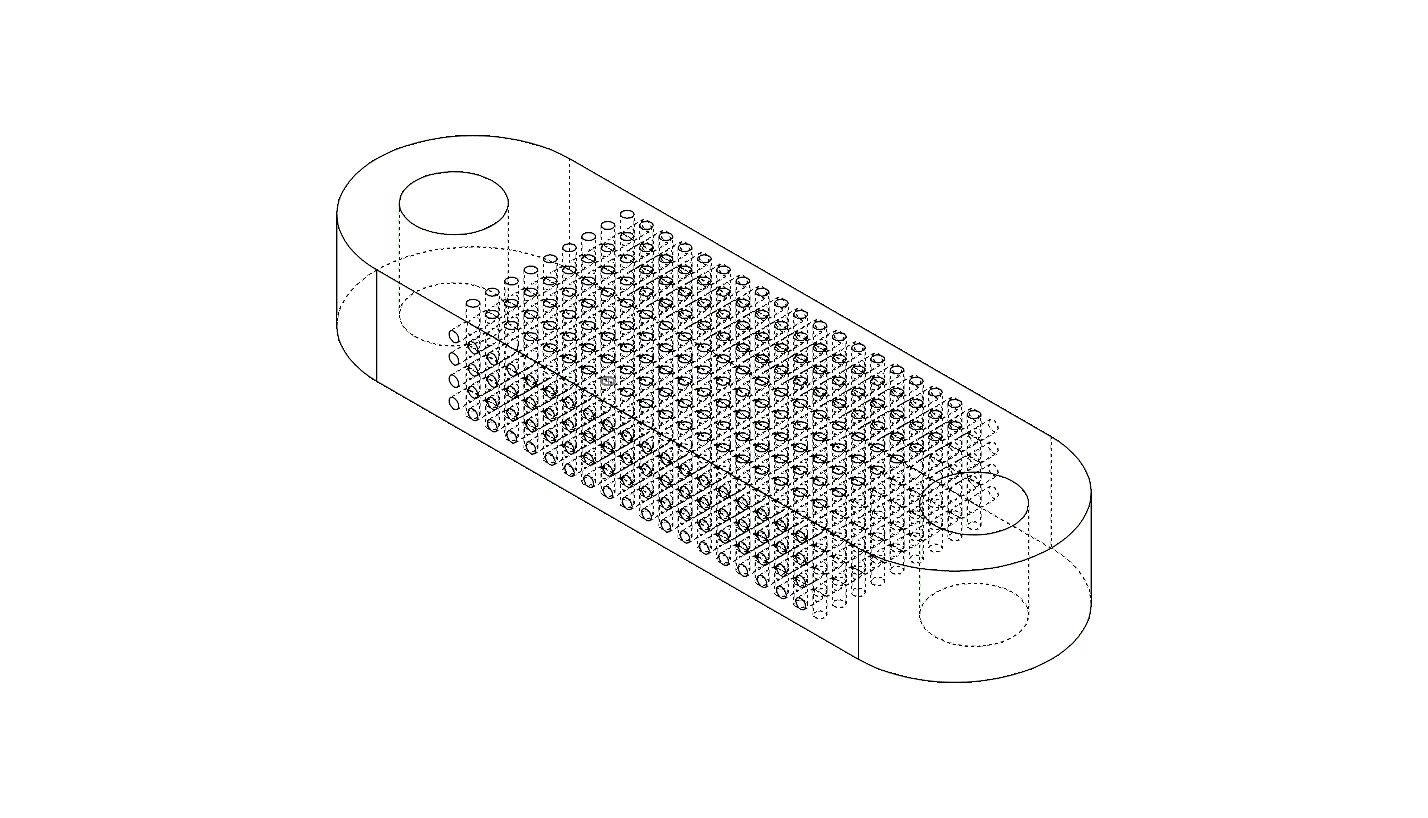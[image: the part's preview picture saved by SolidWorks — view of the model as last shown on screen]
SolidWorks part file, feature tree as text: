
SOLIDWORKS PART (.sldprt)
format: sldprt  version: not decoded by parser v0  size: 1,117,184 bytes
history: native  units: mm
features: sketch x24, cut_extrude x20, pattern_linear x10, extrude x3, material x1 (+13 scaffold rows collapsed)
feature tree (71):
  scaffold x13  (default folders/planes/origin — collapsed)
  material  "Material <not specified>"
  sketch  "Sketch1"
  extrude  "Boss-Extrude1"  Depth=10mm
  sketch  "Sketch2"  dims[D1=~7.810507mm]
  extrude  "Boss-Extrude2"  Depth=10mm
  sketch  "Sketch3"  dims[D1=~9.359973mm]
  extrude  "Boss-Extrude3"  Depth=10mm
  sketch  "Sketch4"  dims[D1=8.0mm]
  cut_extrude  "Cut-Extrude1"  [1 undecoded]
  sketch  "Sketch5"  dims[D1=~3.853714mm]
  cut_extrude  "Cut-Extrude2"  [1 undecoded]
  sketch  "Sketch6"  dims[D1=~0.81725mm]
  cut_extrude  "Cut-Extrude3"  [1 undecoded]
  sketch  "Sketch7"  dims[D1=~1.056004mm]
  cut_extrude  "Cut-Extrude4"  [1 undecoded]
  sketch  "Sketch8"  dims[D1=~0.821133mm]
  cut_extrude  "Cut-Extrude5"  [1 undecoded]
  sketch  "Sketch9"  dims[D1=~1.176837mm]
  cut_extrude  "Cut-Extrude6"  [1 undecoded]
  sketch  "Sketch10"  dims[D1=~0.670574mm]
  cut_extrude  "Cut-Extrude7"  [1 undecoded]
  sketch  "Sketch11"  dims[D1=~0.862768mm]
  cut_extrude  "Cut-Extrude8"  Depth=10mm
  sketch  "Sketch12"  dims[D1=~0.725265mm]
  cut_extrude  "Cut-Extrude9"  [1 undecoded]
  sketch  "Sketch13"  dims[D1=~0.63802mm]
  cut_extrude  "Cut-Extrude10"  [1 undecoded]
  sketch  "Sketch14"  dims[D1=~1.61086mm]
  sketch  "Sketch15"  dims[D1=~0.437297mm]
  cut_extrude  "Cut-Extrude14"  [1 undecoded]
  pattern_linear  "LPattern2"  Count1=1 Count2=11 Spacing1=2mm Spacing2=2mm
  sketch  "Sketch16"  dims[D1=~0.443199mm]
  cut_extrude  "Cut-Extrude15"  [1 undecoded]
  pattern_linear  "LPattern3"  Count1=19 Count2=1 Spacing1=2mm Spacing2=2mm
  sketch  "Sketch17"  dims[D1=~0.884621mm]
  cut_extrude  "Cut-Extrude16"  [1 undecoded]
  pattern_linear  "LPattern4"  Count1=19 Count2=1 Spacing1=2mm Spacing2=2mm
  sketch  "Sketch18"  dims[D1=~0.884621mm]
  cut_extrude  "Cut-Extrude17"  [1 undecoded]
  sketch  "Sketch19"  dims[D1=~1.005556mm]
  cut_extrude  "Cut-Extrude18"  [1 undecoded]
  sketch  "Sketch20"  dims[D1=~1.563536mm]
  cut_extrude  "Cut-Extrude19"  [1 undecoded]
  pattern_linear  "LPattern5"  Count1=19 Count2=1 Spacing1=2mm Spacing2=2mm
  pattern_linear  "LPattern6"  Count1=19 Count2=1 Spacing1=2mm Spacing2=2mm
  pattern_linear  "LPattern7"  Count1=19 Count2=1 Spacing1=2mm Spacing2=2mm
  sketch  "Sketch21"  dims[D1=~0.790313mm]
  cut_extrude  "Cut-Extrude20"  [1 undecoded]
  sketch  "Sketch22"  dims[D1=~0.575532mm]
  cut_extrude  "Cut-Extrude21"  [1 undecoded]
  sketch  "Sketch23"  dims[D1=~0.559483mm]
  cut_extrude  "Cut-Extrude22"  [1 undecoded]
  pattern_linear  "LPattern8"  Count1=19 Count2=1 Spacing1=2mm Spacing2=2mm
  pattern_linear  "LPattern9"  Count1=19 Count2=1 Spacing1=2mm Spacing2=2mm
  pattern_linear  "LPattern10"  Count1=19 Count2=1 Spacing1=2mm Spacing2=2mm
  sketch  "Sketch25"  dims[D1=~0.511416mm]
  cut_extrude  "Cut-Extrude24"  [1 undecoded]
  pattern_linear  "LPattern13"  Count1=4 Count2=19 Spacing1=2mm Spacing2=2mm
decode coverage: 37 of 57 modeling features carry decoded parameters
note: ~ marks probable driven/reference dimensions
note: 19 parameter values undecoded
summary: no parameter record found for 19 features
note: suppression state not decoded; provenance and decode notes live in map.json
